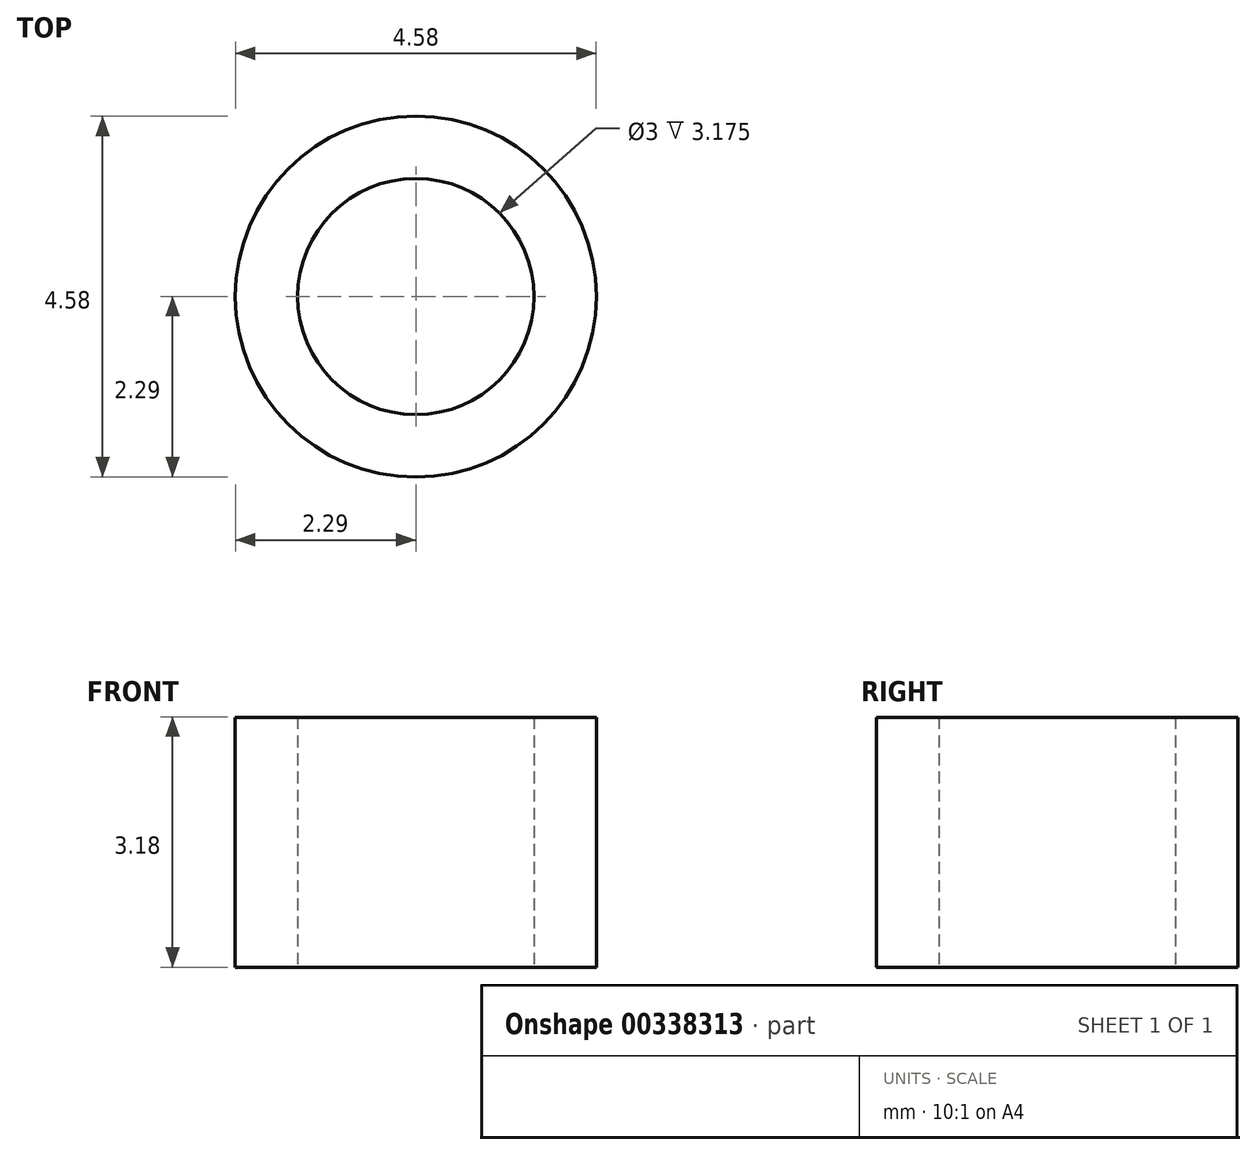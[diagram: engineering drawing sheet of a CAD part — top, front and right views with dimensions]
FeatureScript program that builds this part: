
annotation { "Feature Type Name" : "Feature", "Feature Type Description" : "" }
export const myFeature = defineFeature(function(context is Context, id is Id, definition is map)
    precondition{}
    {
        {
            var Q0;
            Q0=qCreatedBy(makeId("Top.planeOp"),FACE);
            var sketch = newSketch(context, id + "F0", { "sketchPlane" : qUnion([Q0])});
            skCircle(sketch, "E0", {"center": v(0, 0) * mm, "radius": 1.5 * mm});
            skCircle(sketch, "E1", {"center": v(0, 0) * mm, "radius": 2.3 * mm});
            skSolve(sketch);
        }
        {
            var Q0;
            Q0=qSketchRegion(id+"F0",true);
            extrude(context, id + "F1", {"entities" : qUnion([Q0]), "depth" : 3.17 * mm});
        }
    });
